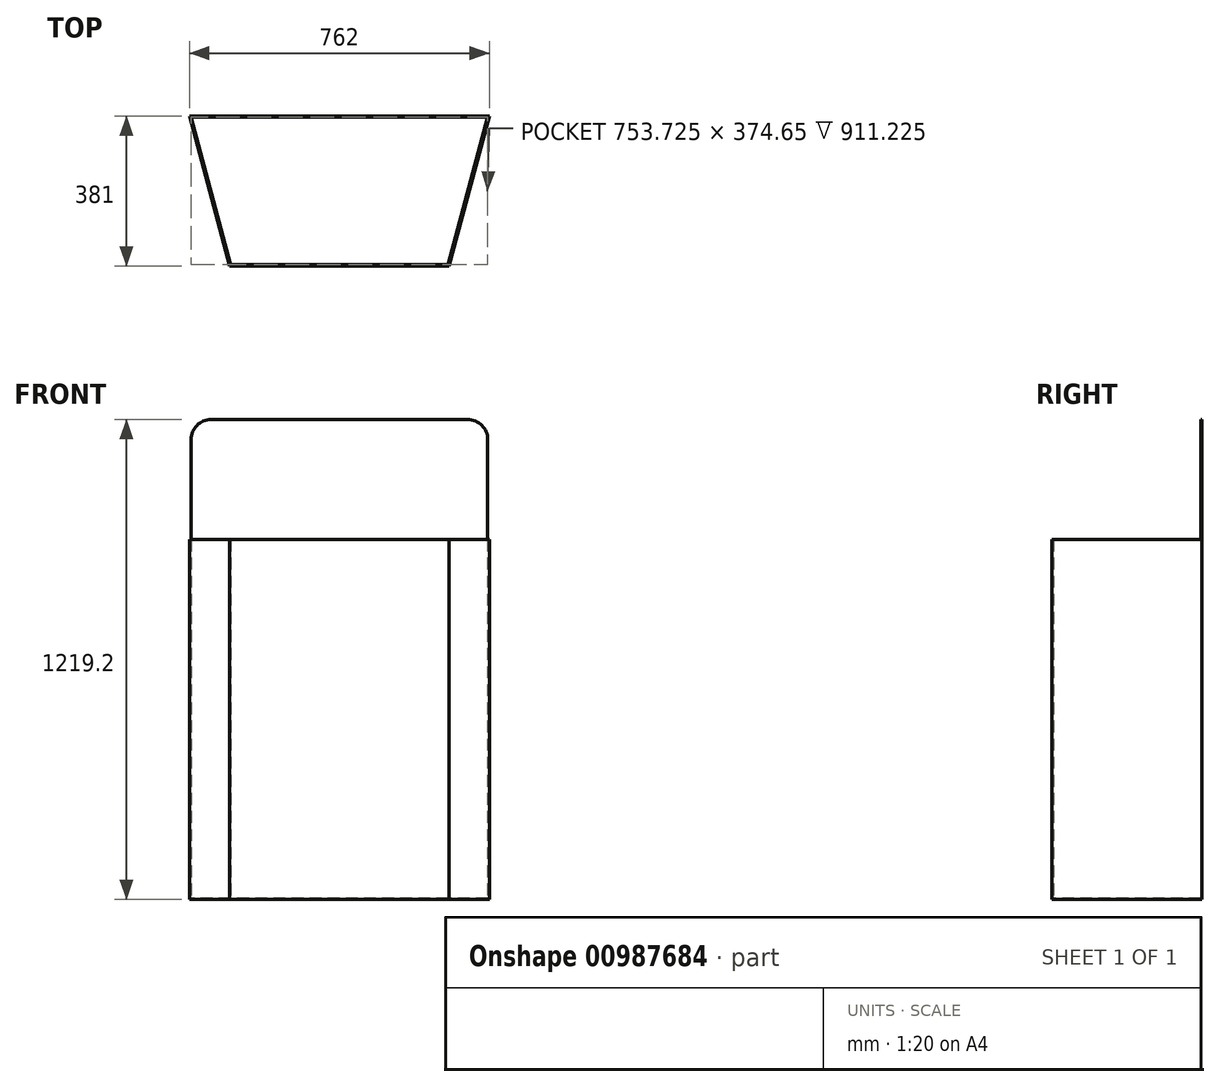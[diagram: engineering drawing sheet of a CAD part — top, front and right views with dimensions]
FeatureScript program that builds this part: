
annotation { "Feature Type Name" : "Feature", "Feature Type Description" : "" }
export const myFeature = defineFeature(function(context is Context, id is Id, definition is map)
    precondition{}
    {
        {
            var Q0;
            Q0=qCreatedBy(makeId("Top.planeOp"),FACE);
            var sketch = newSketch(context, id + "F0", { "sketchPlane" : qUnion([Q0])});
            skLineSegment(sketch, "E0", {"start": v(381, 0) * mm, "end": v(278.91, -381) * mm});
            skLineSegment(sketch, "E1", {"start": v(278.91, -381) * mm, "end": v(-278.91, -381) * mm});
            skLineSegment(sketch, "E2", {"start": v(-278.91, -381) * mm, "end": v(-381, 0) * mm});
            skLineSegment(sketch, "E3", {"start": v(-381, 0) * mm, "end": v(381, 0) * mm});
            skSolve(sketch);
        }
        {
            var Q0;
            Q0 = qSketchRegion(id + "F0", true);
            extrude(context, id + "F1", {"entities" : qUnion([Q0]), "depth" : 914.4 * mm, "offsetDistance" : 25.4 * mm});
        }
        {
            var Q0;
            Q0=makeQuery(id+"F1.opExtrude","CAP_FACE",FACE,{"disambiguationData":[OSD([sQuery(id+"F0.wireOp",EDGE,"E0"),sQuery(id+"F0.wireOp",EDGE,"E1"),sQuery(id+"F0.wireOp",EDGE,"E2"),sQuery(id+"F0.wireOp",EDGE,"E3")])],"isStart":false});
            shell(context, id + "F2", {"entities" : qUnion([Q0]), "thickness" : 3.17 * mm});
        }
        {
            var Q0;
            Q0=makeQuery(id+"F1.opExtrude","CAP_FACE",FACE,{"disambiguationData":[OSD([sQuery(id+"F0.wireOp",EDGE,"E0"),sQuery(id+"F0.wireOp",EDGE,"E1"),sQuery(id+"F0.wireOp",EDGE,"E2"),sQuery(id+"F0.wireOp",EDGE,"E3")])],"isStart":false});
            var sketch = newSketch(context, id + "F3", { "sketchPlane" : qUnion([Q0])});
            skLineSegment(sketch, "E4.bottom", {"start": v(-376.86, -3.17) * mm, "end": v(376.86, -3.17) * mm});
            skLineSegment(sketch, "E4.top", {"start": v(-376.86, 0) * mm, "end": v(376.86, 0) * mm});
            skLineSegment(sketch, "E4.left", {"start": v(-376.86, -3.17) * mm, "end": v(-376.86, 0) * mm});
            skLineSegment(sketch, "E4.right", {"start": v(376.86, -3.17) * mm, "end": v(376.86, 0) * mm});
            skSolve(sketch);
        }
        {
            var Q0;
            Q0 = qSketchRegion(id + "F3", true);
            extrude(context, id + "F4", {"entities" : qUnion([Q0]), "operationType" : NewBodyOperationType.ADD, "depth" : 304.8 * mm, "offsetDistance" : 25.4 * mm});
        }
        {
            var Q0;
            Q0=makeQuery(id+"F4.opExtrude","CAP_EDGE",EDGE,{"disambiguationData":[OSD([sQuery(id+"F3.wireOp",EDGE,"E4.right")])],"isStart":false});
            var Q1;
            Q1=makeQuery(id+"F4.opExtrude","CAP_EDGE",EDGE,{"disambiguationData":[OSD([sQuery(id+"F3.wireOp",EDGE,"E4.left")])],"isStart":false});
            fillet(context, id + "F5", {"entities" : qUnion([Q0, Q1]), "tangentPropagation" : true, "radius" : 50.8 * mm, "defaultsChanged" : true, "vertexSettings" : [], "allowEdgeOverflow" : false});
        }
    });
